# Revit family: Single Skin Roofing_Brownie Blanket (STC 30_Uvalue 0.46) (1)
name_source: partatom
category: Generic Models
units: mm (PartAtom-declared; Revit-internal decimal feet)

## family parameters
Can host rebar = No
Cut with Voids When Loaded = No
Host = Face
Part Type = Normal
Room Calculation Point = No
Round Connector Dimension = Use Diameter
Shared = No

## types (4) — shared parameters
Actual Width (mm) = 3000 mm  [stored 9.84252 ft]
Aluminium foil = Aluminium foil (Double Sided)
ArrayNum = 3
ArrayNum (Top Skin) = 9
Description = ECOWOOL Brownie blanket and slabs are resilient, non-combustible, glass mineral wool products, supplied at roofing and walling application for residential and commercial building
Insulation = BROWNIE BLANKET
Insulation Density = 16 kg/m³
Length (mm) = 2000 mm  [stored 6.56168 ft]
Length Insulation = 2000 mm  [stored 6.56168 ft]
Manufacturer = PGF Insulation Sdn. Bhd.
ProVisSingle (Top Skin) = No
ProfArrN = 3
ProfArrN (Top Skin) = 9
ProfVisDouble = Yes
ProfVisDouble (Top Skin) = Yes
ProfVisSingle = No
SubL = 2805 mm  [stored 9.20276 ft]
SubL (Top Skin) = 2718 mm  [stored 8.91732 ft]
SubW = 3740 mm
SubW (Top Skin) = 3020 mm  [stored 9.90814 ft]
Type of Insulation = Glass Mineral Wool Blanket
URL = www.ecowool.com.my
zero-valued in all types: Default Elevation

## per-type parameters (varying)
| type | A | ECOWOOL Product thickness in mm | Finish | Insulation Density (kg/m3) | Insulation thk. (mm) | Remarks | STC in dB | System Description | Thermal K Value | Thermal R Value | Total System Thickness-mm | Typical weight of ECOWOOL-Kg/M2 | U-Value W/m2k |
| 75mm | 76.5 mm  [stored 0.250984 ft] |  | ZINCALUME® ULTRA -  ACTIVATE™ | 32 mm  [stored 0.104987 ft] | 75 mm |  | 0 |  | 0.0342 | 1.35 | 0 mm  [stored 0 ft] | 0 mm  [stored 0 ft] | 0 mm  [stored 0 ft] |
| ECOWOOL EWBL2.00 | 51.5 mm  [stored 0.168963 ft] | 75 x 16 Kg/m3 | Metal Deck Roofing | 16 mm  [stored 0.0524934 ft] | 75 mm | Single skin metal roof for Shop Office, Indoor Sport. Commonly used in government buildings- classroom, admin blocks, canteen, workshop, multipurpose hall, stores. | 30 | 1. Aluminum Foil
2. Ecowool  EWBL2.00
3. 75mm Z spacer                           
4. Metal Deck/ Zincalume Liner | 0.0366 | 2 | 110 mm  [stored 0.360892 ft] | 1.2 mm  [stored 0.00393701 ft] | 0.46 mm  [stored 0.00150919 ft] |
| 85mm | 86.5 mm  [stored 0.283793 ft] |  | ZINCALUME® ULTRA -  ACTIVATE™ | 32 mm  [stored 0.104987 ft] | 85 mm  [stored 0.278871 ft] |  | 0 |  | 0.0342 | 1.35 | 0 mm  [stored 0 ft] | 0 mm  [stored 0 ft] | 0 mm  [stored 0 ft] |
| 100mm | 101.5 mm  [stored 0.333005 ft] |  | ZINCALUME® ULTRA -  ACTIVATE™ | 32 mm  [stored 0.104987 ft] | 100 mm  [stored 0.328084 ft] |  | 0 |  | 0.0342 | 1.35 | 0 mm  [stored 0 ft] | 0 mm  [stored 0 ft] | 0 mm  [stored 0 ft] |

note: [stored X ft] marks values corroborated as IEEE doubles in the binary element streams (Revit-internal decimal feet)

## geometry (parser evidence)
native form markers: Sweep x27
no freeform markers — native parametric forms only
